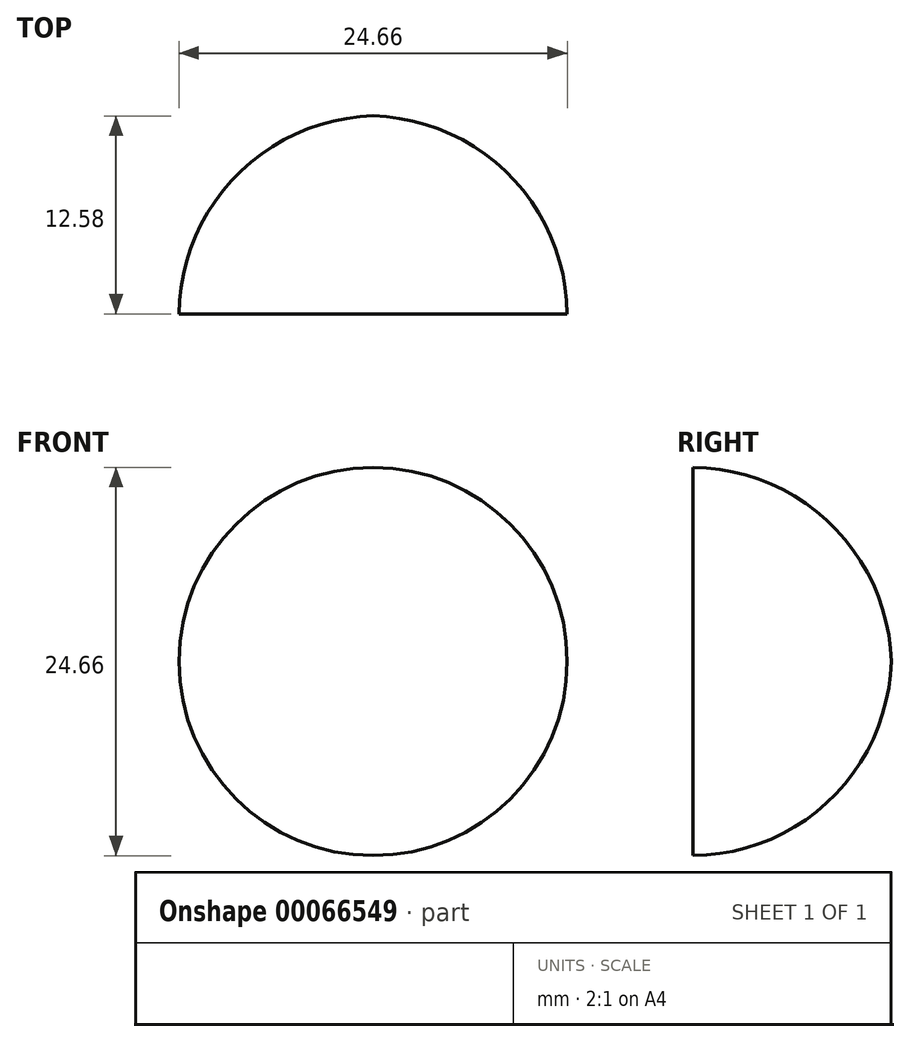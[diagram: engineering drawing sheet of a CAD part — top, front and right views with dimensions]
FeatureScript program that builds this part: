
annotation { "Feature Type Name" : "Feature", "Feature Type Description" : "" }
export const myFeature = defineFeature(function(context is Context, id is Id, definition is map)
    precondition{}
    {
        {
            var Q0;
            Q0=qCreatedBy(makeId("Right.planeOp"),FACE);
            var sketch = newSketch(context, id + "F0", { "sketchPlane" : qUnion([Q0])});
            skLineSegment(sketch, "E0", {"start": v(0, 12.33) * mm, "end": v(0, 0) * mm});
            skArc(sketch, "E1", {"start": v(12.58, 0) * mm, "mid": v(8.77, 8.7) * mm, "end": v(0, 12.33) * mm});
            skLineSegment(sketch, "E2", {"start": v(12.58, 0) * mm, "end": v(0, 0) * mm});
            skSolve(sketch);
        }
        {
            var Q0;
            Q0=qSketchRegion(id+"Fc65ZHBwZbTgPMm_0",true);
            var Q1;
            Q1=makeQuery(id+"F0.imprint","IMPRINT",FACE,{"disambiguationData":[TD([[makeQuery(id+"F0.imprint","IMPRINT",EDGE,{"derivedFrom":sQuery(id+"F0.wireOp",EDGE,"E0")}),1.0]])]});
            var Q2;
            Q2=sQuery(id+"F0.wireOp",EDGE,"E2");
            revolve(context, id + "F1", {"entities" : qUnion([Q0, Q1]), "axis" : qUnion([Q2]), "revolveType" : RevolveType.FULL});
        }
    });
